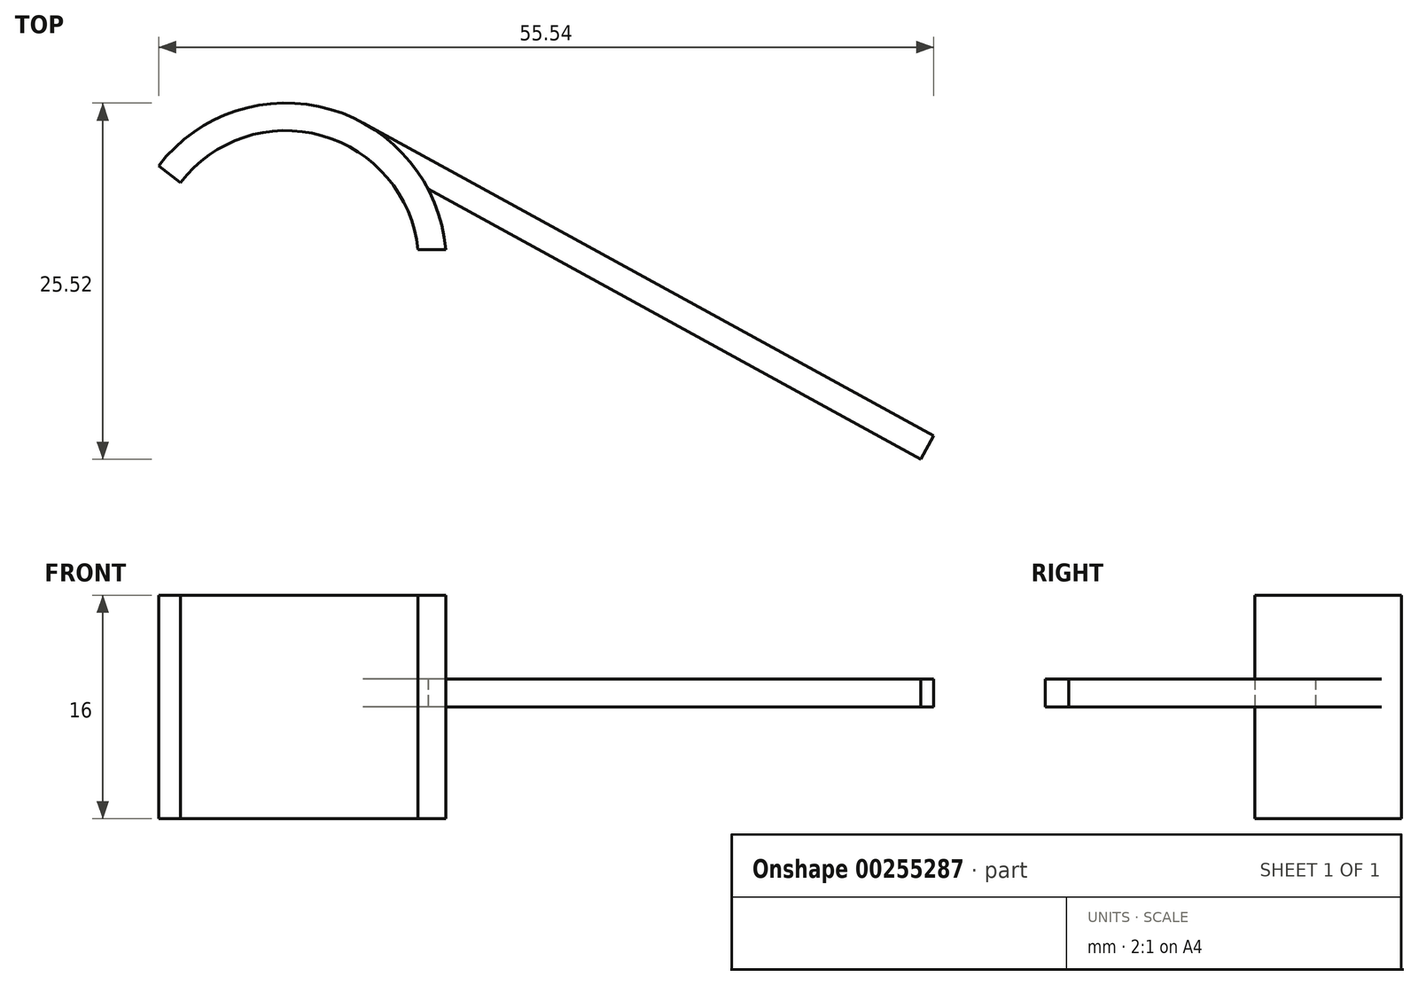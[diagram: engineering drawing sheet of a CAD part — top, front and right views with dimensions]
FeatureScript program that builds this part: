
annotation { "Feature Type Name" : "Feature", "Feature Type Description" : "" }
export const myFeature = defineFeature(function(context is Context, id is Id, definition is map)
    precondition{}
    {
        {
            var Q0;
            Q0=qCreatedBy(makeId("Top.planeOp"),FACE);
            var sketch = newSketch(context, id + "F0", { "sketchPlane" : qUnion([Q0])});
            skCircle(sketch, "E0", {"center": v(0, 0) * mm, "radius": 9.53 * mm});
            skLineSegment(sketch, "E1", {"start": v(-9.12, 7) * mm, "end": v(0, 0) * mm});
            skLineSegment(sketch, "E2", {"start": v(0, 0) * mm, "end": v(-9.12, -7) * mm});
            skLineSegment(sketch, "E3", {"start": v(11.46, 1) * mm, "end": v(9.47, 1) * mm});
            skLineSegment(sketch, "E4", {"start": v(11.46, -1) * mm, "end": v(9.47, -1) * mm});
            skCircle(sketch, "E5", {"center": v(0, 0) * mm, "radius": 11.5 * mm});
            skPoint(sketch, "E6", {"position": v(23.92, 0) * mm});
            skLineSegment(sketch, "E7", {"start": v(23.92, 0) * mm, "end": v(5.53, 10.08) * mm});
            skLineSegment(sketch, "E8", {"start": v(23.92, 0) * mm, "end": v(5.53, -10.08) * mm});
            skPoint(sketch, "E9", {"position": v(19.92, 0) * mm});
            skLineSegment(sketch, "E10", {"start": v(19.92, 0) * mm, "end": v(10.19, 5.34) * mm});
            skLineSegment(sketch, "E11", {"start": v(19.92, 0) * mm, "end": v(10.19, -5.34) * mm});
            skLineSegment(sketch, "E12", {"start": v(19.92, 0) * mm, "end": v(45.5, -14.02) * mm});
            skLineSegment(sketch, "E13", {"start": v(23.92, 0) * mm, "end": v(46.42, -12.33) * mm});
            skLineSegment(sketch, "E14", {"start": v(45.5, -14.02) * mm, "end": v(46.42, -12.33) * mm});
            skLineSegment(sketch, "E15", {"start": v(19.92, 0) * mm, "end": v(21.92, 1.1) * mm});
            skCircle(sketch, "E16", {"center": v(0, 0) * mm, "radius": 8.87 * mm});
            skLineSegment(sketch, "E17", {"start": v(8.82, 1) * mm, "end": v(11.46, 1) * mm});
            skLineSegment(sketch, "E18", {"start": v(8.82, -1) * mm, "end": v(11.46, -1) * mm});
            skSolve(sketch);
        }
        {
            var Q0;
            {var subQ5=sQuery(id+"F0.wireOp",EDGE,"E0");var subQ7=sQuery(id+"F0.wireOp",EDGE,"E1");var subQ9=makeQuery(id+"F0.imprint","INTERSECT",VERTEX,{"derivedFrom":[subQ5,subQ7]});Q0=makeQuery(id+"F0.imprint","IMPRINT",FACE,{"disambiguationData":[TD([[makeQuery(id+"F0.imprint","IMPRINT",EDGE,{"disambiguationData":[TD([[subQ9,1.0]])],"derivedFrom":subQ5}),-1.0]])]});}
            extrude(context, id + "F1", {"entities" : qUnion([Q0]), "endBound" : BoundingType.SYMMETRIC, "depth" : 16 * mm});
        }
        {
            var Q0;
            {var subQ3=sQuery(id+"F0.wireOp",EDGE,"E10");Q0=makeQuery(id+"F0.imprint","IMPRINT",FACE,{"disambiguationData":[TD([[makeQuery(id+"F0.imprint","IMPRINT",EDGE,{"derivedFrom":subQ3}),-1.0]])]});}
            var Q1;
            {var subQ3=sQuery(id+"F0.wireOp",EDGE,"E15");Q1=makeQuery(id+"F0.imprint","IMPRINT",FACE,{"disambiguationData":[TD([[makeQuery(id+"F0.imprint","IMPRINT",EDGE,{"derivedFrom":subQ3}),-1.0]])]});}
            var Q2;
            {var subQ0=sQuery(id+"F0.wireOp",EDGE,"E13");Q2=makeQuery(id+"F0.imprint","IMPRINT",FACE,{"disambiguationData":[TD([[makeQuery(id+"F0.imprint","IMPRINT",EDGE,{"derivedFrom":subQ0}),-1.0]])]});}
            extrude(context, id + "F2", {"entities" : qUnion([Q0, Q1, Q2]), "operationType" : NewBodyOperationType.ADD, "depth" : 2 * mm});
        }
    });
